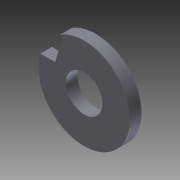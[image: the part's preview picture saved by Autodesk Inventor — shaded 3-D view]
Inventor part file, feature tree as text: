
AUTODESK INVENTOR PART (.ipt)
format: ipt  version: 2014 SP1 (Build 180222100, 222)  size: 88,576 bytes
history: native  units: in
note: dims shown in document units (in); Inventor stores cm internally (conversion verified against a paired STEP export)
features: reference x3, extrude x2, sketch x2
ambient origin geometry x8: Origin, YZ Plane, XZ Plane, XY Plane, X Axis, Y Axis, Z Axis, Center Point
bodies: Solid1 (feature_tree)
feature tree (7):
  extrude  "Extrusion1"  Depth=0.25in
  extrude  "Extrusion2"  Depth=0.08in TaperAngle=0.0deg
  sketch  "Sketch1"  dims[d0=0.625in d1=0.25in]
  sketch  "Sketch2"  dims[d2=0.08in d3=0.0in d4=1.0in d5=0.0in]
  reference  "Reference1"
  reference  "Reference2"
  reference  "Reference3"
